# Revit family: CADS_Vent-Axia_MechEquip_Fan_VSP_SabreSicklePlate_3Ph4P - SUPPLY
name_source: partatom
category: Mechanical Equipment
units: mm (PartAtom-declared; Revit-internal decimal feet)

## family parameters
Always vertical = Yes
Cut with Voids When Loaded = No
OmniClass Number = 23.75.00.00
OmniClass Title = Climate Control (HVAC)
Part Type = Normal
Room Calculation Point = No
Round Connector Dimension = Use Diameter
Shared = No
Work Plane-Based = No

## types (8) — shared parameters
AirflowRateRange = 0.0 L/s
AssemblyPlace = UNKNOWN
AssetType = FIXED
DurationUnit = Year
E = 34 mm
ExteriorInsulation = No
Fitting Type = Ignore
G = 17 mm
GrossWeight = 0.00 kg
HasProtectiveEarth = No
IfcExportAs = IfcFanType
IsExtendedWarranty = No
ManufacturerAddress = Fleming Way
Crawley 
RH10 9YX
Quantity = 1
RatedCurrent = 0 A
RatedVoltage = 0 V
Status = New
WarrantyGuarantor = Vent-Axia Limited
WorkingPressure = 0.0 Pa
zero-valued in all types: CADS_Index, CADS_Usage, Default Elevation, ExpectedServiceLife, NumberOfPoles

## per-type parameters (varying)
| type | A | ModelReference | NominalDiameter | NominalHeight | NominalLength | NominalWidth |
| VSP31534A | 430 mm | OWLET SICKLE PLATE FAN 315 DIA 3PH 4 POLE | 315 mm  [stored 1.03346 ft] | 315 mm  [stored 1.03346 ft] | 84 mm  [stored 0.275591 ft] | 430 mm |
| VSP35534A | 485 mm  [stored 1.59121 ft] | OWLET SICKLE PLATE FAN 355 IDA 3PH 4 POLE | 355 mm | 355 mm | 83 mm | 485 mm  [stored 1.59121 ft] |
| VSP40034A | 549 mm  [stored 1.80118 ft] | OWLET SICKLE PLATE FAN 400DIA 3PH 4 POLE | 400 mm  [stored 1.31234 ft] | 400 mm  [stored 1.31234 ft] | 92 mm | 549 mm  [stored 1.80118 ft] |
| VSP45034A | 575 mm | OWLET SICKLE PLATE FAN 450DIA 3PH 4 POLE | 450 mm  [stored 1.47638 ft] | 450 mm  [stored 1.47638 ft] | 144 mm | 575 mm |
| VSP45036 | 575 mm | SICKLE PLATE FAN 450DIA 3PH 4 POLE | 450 mm  [stored 1.47638 ft] | 450 mm  [stored 1.47638 ft] | 144 mm | 575 mm |
| VSP50034A | 655 mm  [stored 2.14895 ft] | OWLET SICKLE PLATE FAN 500DIA 3 PH 4 POLE | 500 mm  [stored 1.64042 ft] | 500 mm  [stored 1.64042 ft] | 142 mm | 655 mm  [stored 2.14895 ft] |
| VSP56034A | 725 mm  [stored 2.37861 ft] | OWLET SICKLE PLATE FAN 560 DIA 3 PH 4 POLE | 560 mm  [stored 1.83727 ft] | 560 mm  [stored 1.83727 ft] | 163 mm | 725 mm  [stored 2.37861 ft] |
| VSP63034B | 805 mm  [stored 2.64108 ft] | 630MM 3PH 4P SICKLE FAN FN63-VDQ.6N.A7P3 169516 | 630 mm  [stored 2.06693 ft] | 630 mm  [stored 2.06693 ft] | 160 mm | 805 mm  [stored 2.64108 ft] |

note: column(s) folded — value = type name in every type: ModelNumber

note: [stored X ft] marks values corroborated as IEEE doubles in the binary element streams (Revit-internal decimal feet)

## geometry (parser evidence)
native form markers: Sweep x12
no freeform markers — native parametric forms only
